# Revit family: Haier-AP140S2SK1FA(H)
name_source: partatom
category: 机械设备
revit_build: Autodesk Revit 2018 (Build: 20170223_1515(x64)
units: mm (PartAtom-declared; Revit-internal decimal feet)

## family parameters
OmniClass 标题 = Air Handling Units
OmniClass 编号 = 23.75.35.14
共享 = 否
加载时剪切的空心 = 否
圆形连接件大小 = 使用直径
基于工作平面 = 否
总是垂直 = 是
房间计算点 = 否
零件类型 = 标准

## types (1)
- AP140S2SK1FA(H)
    Button = silver gray
    Electrical Supply Type = 1 /220～240/50/60HZ
    Heating capacity = 15KW
    Model Number = AP140S2SK1FA(H)
    Nominal Height = 1850mm
    Nominal Length = 600mm
    Nominal Width = 350mm
    Nominal frequency range = 50/60 HZ
    Output cooling = 13 kW
    Output heating = 15 kW
    RatedVoltage = 1 /220～240V
    Refrigerant gas pipe size = 16
    Refrigerant liquid pipe size = 10  [stored 0.0328084 ft]
    Refrigerant pipe = copper
    Size = 1850×600×350mm
    Sound power level = 66dB
    Sound pressure level = 52/49/46dB
    Structure = White smoke
    UnitDepth = 350  [stored 1.14829 ft]
    UnitHeight = 1850  [stored 6.06955 ft]
    UnitWidth = 600  [stored 1.9685 ft]
    Weight = 61kg
    refrigerant = R32
    制造商 = Haier
    型号 = AP140S2SK1FA(H)

note: [stored X ft] marks values corroborated as IEEE doubles in the binary element streams (Revit-internal decimal feet)
